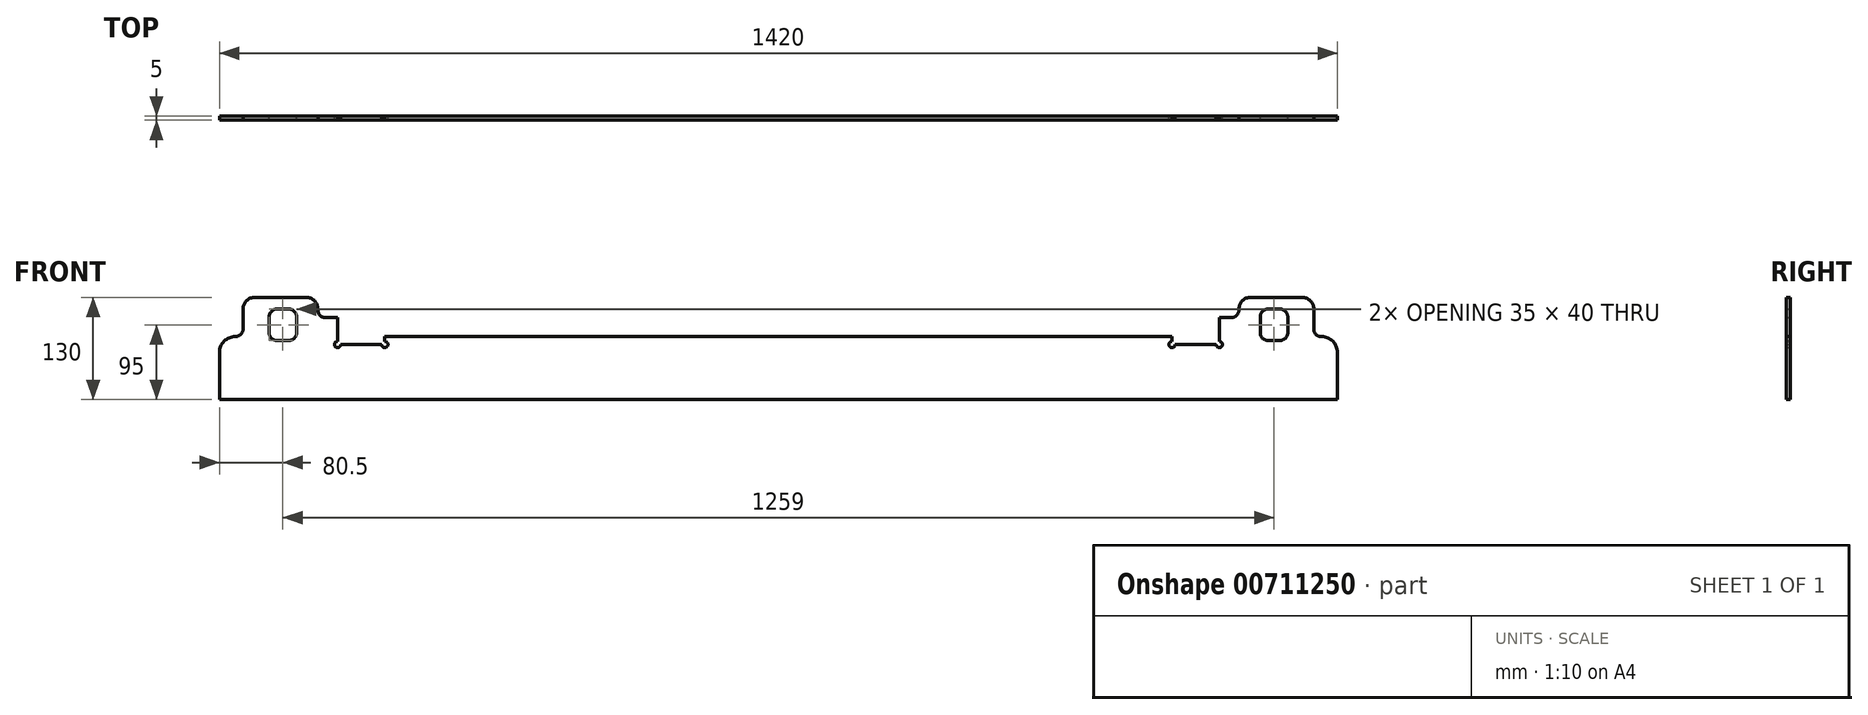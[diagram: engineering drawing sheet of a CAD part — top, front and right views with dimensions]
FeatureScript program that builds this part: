
annotation { "Feature Type Name" : "Feature", "Feature Type Description" : "" }
export const myFeature = defineFeature(function(context is Context, id is Id, definition is map)
    precondition{}
    {
        {
            var Q0;
            Q0=qCreatedBy(makeId("Front.planeOp"),FACE);
            var sketch = newSketch(context, id + "F0", { "sketchPlane" : qUnion([Q0])});
            skLineSegment(sketch, "E0.bottom", {"start": v(-690, 40) * mm, "end": v(-690, 40) * mm});
            skLineSegment(sketch, "E0.top", {"start": v(-710, -40) * mm, "end": v(710, -40) * mm});
            skLineSegment(sketch, "E0.left", {"start": v(-710, 20) * mm, "end": v(-710, -40) * mm});
            skPoint(sketch, "E0.middle", {"position": v(0, 0) * mm});
            skLineSegment(sketch, "E1.0", {"start": v(-500, 40) * mm, "end": v(-500, 34) * mm});
            skLineSegment(sketch, "E2.0", {"start": v(-556, 30) * mm, "end": v(-504, 30) * mm});
            skLineSegment(sketch, "E3.0", {"start": v(500, 40) * mm, "end": v(500, 34) * mm});
            skLineSegment(sketch, "E4.trimOffspring", {"start": v(504, 30) * mm, "end": v(556, 30) * mm});
            skLineSegment(sketch, "E5.trimOffspring", {"start": v(-500, 40) * mm, "end": v(500, 40) * mm});
            skPoint(sketch, "E6.visualSharp", {"position": v(-710, 40) * mm});
            skArc(sketch, "E6.filletArc", {"start": v(-690, 40) * mm, "mid": v(-704.14, 34.14) * mm, "end": v(-710, 20) * mm});
            skArc(sketch, "E7", {"start": v(-560, 34) * mm, "mid": v(-562.83, 27.17) * mm, "end": v(-556, 30) * mm});
            skArc(sketch, "E8", {"start": v(-504, 30) * mm, "mid": v(-497.17, 27.17) * mm, "end": v(-500, 34) * mm});
            skArc(sketch, "E9", {"start": v(556, 30) * mm, "mid": v(562.83, 27.17) * mm, "end": v(560, 34) * mm});
            skArc(sketch, "E10", {"start": v(500, 34) * mm, "mid": v(497.17, 27.17) * mm, "end": v(504, 30) * mm});
            skLineSegment(sketch, "E11.0", {"start": v(-665, 90) * mm, "end": v(-600, 90) * mm});
            skLineSegment(sketch, "E12", {"start": v(-680, 50) * mm, "end": v(-680, 75) * mm});
            skLineSegment(sketch, "E13", {"start": v(-575, 64) * mm, "end": v(-560, 64) * mm});
            skLineSegment(sketch, "E14", {"start": v(-585, 74) * mm, "end": v(-585, 75) * mm});
            skLineSegment(sketch, "E15", {"start": v(-560, 64) * mm, "end": v(-560, 34) * mm});
            skPoint(sketch, "E16.visualSharp", {"position": v(-680, 40) * mm});
            skArc(sketch, "E16.filletArc", {"start": v(-690, 40) * mm, "mid": v(-682.93, 42.93) * mm, "end": v(-680, 50) * mm});
            skPoint(sketch, "E17.visualSharp", {"position": v(-680, 90) * mm});
            skArc(sketch, "E17.filletArc", {"start": v(-665, 90) * mm, "mid": v(-675.6, 85.6) * mm, "end": v(-680, 75) * mm});
            skPoint(sketch, "E18.visualSharp", {"position": v(-585, 90) * mm});
            skArc(sketch, "E18.filletArc", {"start": v(-585, 75) * mm, "mid": v(-589.4, 85.6) * mm, "end": v(-600, 90) * mm});
            skPoint(sketch, "E19.visualSharp", {"position": v(-585, 64) * mm});
            skArc(sketch, "E19.filletArc", {"start": v(-585, 74) * mm, "mid": v(-582.07, 66.93) * mm, "end": v(-575, 64) * mm});
            skLineSegment(sketch, "E20.bottom", {"start": v(-637, 75) * mm, "end": v(-622, 75) * mm});
            skLineSegment(sketch, "E20.top", {"start": v(-637, 35) * mm, "end": v(-622, 35) * mm});
            skLineSegment(sketch, "E20.left", {"start": v(-647, 65) * mm, "end": v(-647, 45) * mm});
            skLineSegment(sketch, "E20.right", {"start": v(-612, 65) * mm, "end": v(-612, 45) * mm});
            skPoint(sketch, "E21", {"position": v(-736.23, 53.72) * mm});
            skPoint(sketch, "E22.visualSharp", {"position": v(-647, 75) * mm});
            skArc(sketch, "E22.filletArc", {"start": v(-637, 75) * mm, "mid": v(-644.07, 72.07) * mm, "end": v(-647, 65) * mm});
            skPoint(sketch, "E23.visualSharp", {"position": v(-647, 35) * mm});
            skArc(sketch, "E23.filletArc", {"start": v(-647, 45) * mm, "mid": v(-644.07, 37.93) * mm, "end": v(-637, 35) * mm});
            skPoint(sketch, "E24.visualSharp", {"position": v(-612, 75) * mm});
            skArc(sketch, "E24.filletArc", {"start": v(-612, 65) * mm, "mid": v(-614.93, 72.07) * mm, "end": v(-622, 75) * mm});
            skPoint(sketch, "E25.visualSharp", {"position": v(-612, 35) * mm});
            skArc(sketch, "E25.filletArc", {"start": v(-622, 35) * mm, "mid": v(-614.93, 37.93) * mm, "end": v(-612, 45) * mm});
            skLineSegment(sketch, "E26.MirrorCS", {"start": v(585, 74) * mm, "end": v(585, 75) * mm});
            skArc(sketch, "E27.MirrorCS", {"start": v(637, 75) * mm, "mid": v(644.07, 72.07) * mm, "end": v(647, 65) * mm});
            skLineSegment(sketch, "E28.MirrorCS", {"start": v(647, 65) * mm, "end": v(647, 45) * mm});
            skArc(sketch, "E29.MirrorCS", {"start": v(690, 40) * mm, "mid": v(682.93, 42.93) * mm, "end": v(680, 50) * mm});
            skLineSegment(sketch, "E30.MirrorCS", {"start": v(637, 75) * mm, "end": v(622, 75) * mm});
            skArc(sketch, "E31.MirrorCS", {"start": v(612, 65) * mm, "mid": v(614.93, 72.07) * mm, "end": v(622, 75) * mm});
            skArc(sketch, "E32.MirrorCS", {"start": v(585, 74) * mm, "mid": v(582.07, 66.93) * mm, "end": v(575, 64) * mm});
            skArc(sketch, "E33.MirrorCS", {"start": v(647, 45) * mm, "mid": v(644.07, 37.93) * mm, "end": v(637, 35) * mm});
            skLineSegment(sketch, "E34.MirrorCS", {"start": v(637, 35) * mm, "end": v(622, 35) * mm});
            skArc(sketch, "E35.MirrorCS", {"start": v(622, 35) * mm, "mid": v(614.93, 37.93) * mm, "end": v(612, 45) * mm});
            skLineSegment(sketch, "E36.MirrorCS", {"start": v(575, 64) * mm, "end": v(560, 64) * mm});
            skLineSegment(sketch, "E37.MirrorCS", {"start": v(612, 65) * mm, "end": v(612, 45) * mm});
            skArc(sketch, "E38.MirrorCS", {"start": v(665, 90) * mm, "mid": v(675.6, 85.6) * mm, "end": v(680, 75) * mm});
            skArc(sketch, "E39.MirrorCS", {"start": v(585, 75) * mm, "mid": v(589.4, 85.6) * mm, "end": v(600, 90) * mm});
            skPoint(sketch, "E40.MirrorP", {"position": v(647, 75) * mm});
            skArc(sketch, "E41.MirrorCS", {"start": v(690, 40) * mm, "mid": v(704.14, 34.14) * mm, "end": v(710, 20) * mm});
            skLineSegment(sketch, "E42.MirrorCS", {"start": v(680, 50) * mm, "end": v(680, 75) * mm});
            skLineSegment(sketch, "E43.MirrorCS", {"start": v(710, 20) * mm, "end": v(710, -40) * mm});
            skPoint(sketch, "E44.MirrorP", {"position": v(680, 90) * mm});
            skPoint(sketch, "E45.MirrorP", {"position": v(585, 90) * mm});
            skPoint(sketch, "E46.MirrorP", {"position": v(585, 64) * mm});
            skPoint(sketch, "E47.MirrorP", {"position": v(612, 75) * mm});
            skPoint(sketch, "E48.MirrorP", {"position": v(710, 40) * mm});
            skPoint(sketch, "E49.MirrorP", {"position": v(680, 40) * mm});
            skPoint(sketch, "E50.MirrorP", {"position": v(612, 35) * mm});
            skLineSegment(sketch, "E51.MirrorCS", {"start": v(560, 64) * mm, "end": v(560, 34) * mm});
            skLineSegment(sketch, "E52.MirrorCS", {"start": v(665, 90) * mm, "end": v(600, 90) * mm});
            skPoint(sketch, "E53.MirrorP", {"position": v(736.23, 53.72) * mm});
            skPoint(sketch, "E54.MirrorP", {"position": v(647, 35) * mm});
            skSolve(sketch);
        }
        {
            var Q0;
            Q0=makeQuery(id+"F0.imprint","IMPRINT",FACE,{"disambiguationData":[TD([[makeQuery(id+"F0.imprint","IMPRINT",EDGE,{"derivedFrom":sQuery(id+"F0.wireOp",EDGE,"E0.top")}),1.0]])]});
            extrude(context, id + "F1", {"entities" : qUnion([Q0]), "depth" : 5 * mm, "offsetDistance" : 25 * mm});
        }
    });
